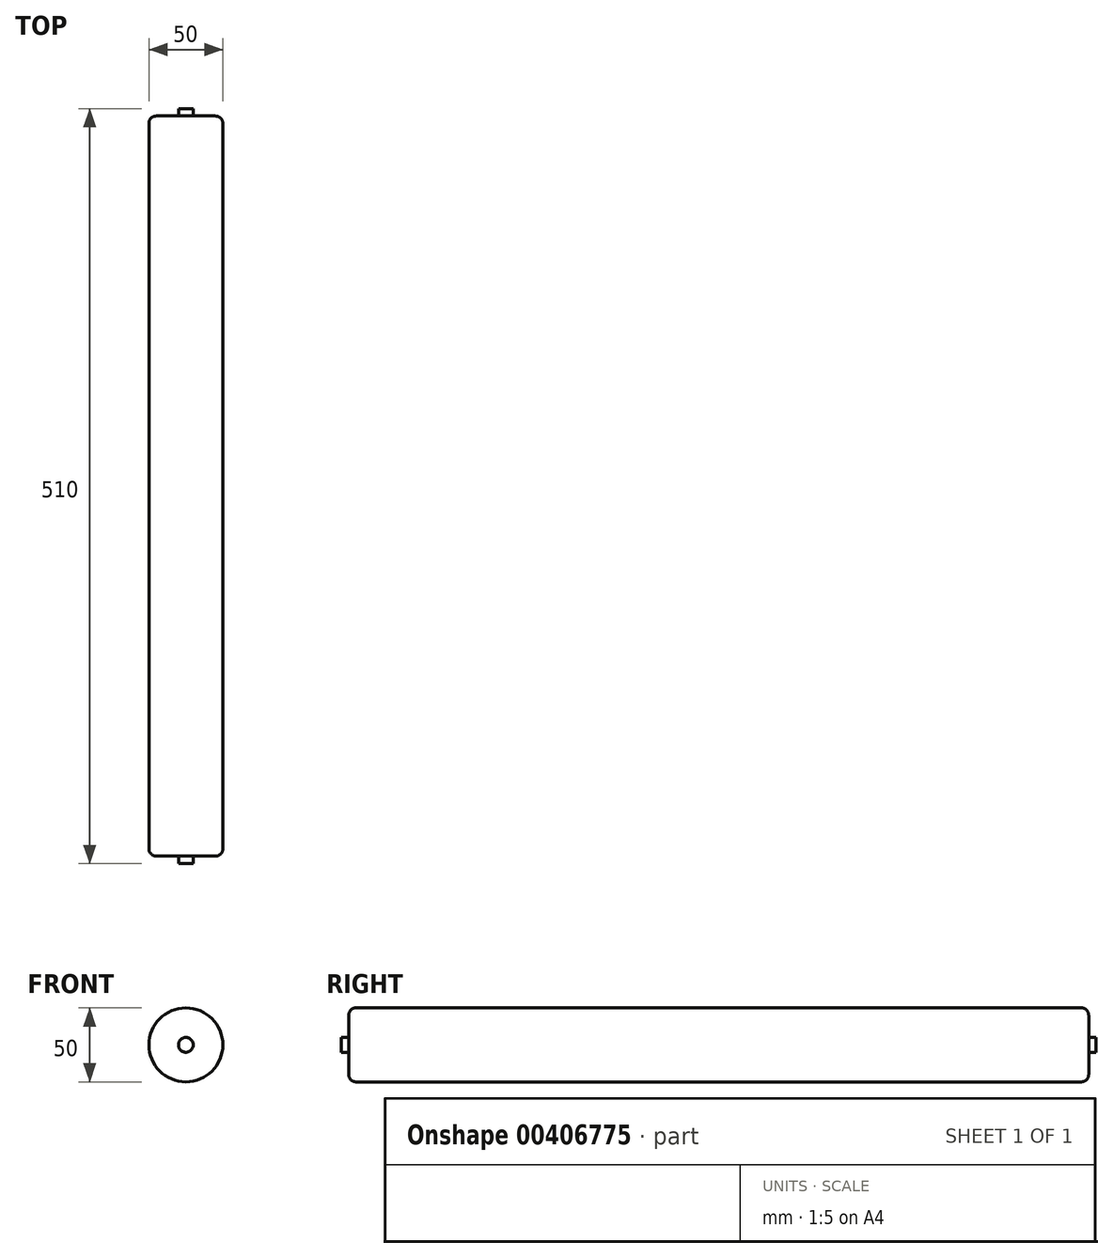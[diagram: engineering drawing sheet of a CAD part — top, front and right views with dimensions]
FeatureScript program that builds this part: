
annotation { "Feature Type Name" : "Feature", "Feature Type Description" : "" }
export const myFeature = defineFeature(function(context is Context, id is Id, definition is map)
    precondition{}
    {
        {
            var Q0;
            Q0=qCreatedBy(makeId("Front.planeOp"),FACE);
            var sketch = newSketch(context, id + "F0", { "sketchPlane" : qUnion([Q0])});
            skCircle(sketch, "E0", {"center": v(41.25, 34.25) * mm, "radius": 25 * mm});
            skSolve(sketch);
        }
        {
            var Q0;
            Q0=makeQuery(id+"F0.imprint","IMPRINT",FACE,{"disambiguationData":[TD([[makeQuery(id+"F0.imprint","IMPRINT",EDGE,{"derivedFrom":sQuery(id+"F0.wireOp",EDGE,"E0")}),1.0]])]});
            extrude(context, id + "F1", {"entities" : qUnion([Q0]), "depth" : 500 * mm});
        }
        {
            var Q0;
            Q0=makeQuery(id+"F1.opExtrude","CAP_FACE",FACE,{"disambiguationData":[OSD([sQuery(id+"F0.wireOp",EDGE,"E0")])],"isStart":true});
            var sketch = newSketch(context, id + "F2", { "sketchPlane" : qUnion([Q0])});
            skCircle(sketch, "E1", {"center": v(-41.25, 34.25) * mm, "radius": 5 * mm});
            skSolve(sketch);
        }
        {
            var Q0;
            Q0=makeQuery(id+"F2.imprint","IMPRINT",FACE,{"disambiguationData":[TD([[makeQuery(id+"F2.imprint","IMPRINT",EDGE,{"derivedFrom":sQuery(id+"F2.wireOp",EDGE,"E1")}),1.0]])]});
            extrude(context, id + "F3", {"entities" : qUnion([Q0]), "operationType" : NewBodyOperationType.ADD, "depth" : 5 * mm});
        }
        {
            var Q0;
            Q0=makeQuery(id+"F1.opExtrude","CAP_FACE",FACE,{"disambiguationData":[OSD([sQuery(id+"F0.wireOp",EDGE,"E0")])],"isStart":false});
            var sketch = newSketch(context, id + "F4", { "sketchPlane" : qUnion([Q0])});
            skCircle(sketch, "E2", {"center": v(41.25, 34.25) * mm, "radius": 5 * mm});
            skSolve(sketch);
        }
        {
            var Q0;
            Q0=makeQuery(id+"F4.imprint","IMPRINT",FACE,{"disambiguationData":[TD([[makeQuery(id+"F4.imprint","IMPRINT",EDGE,{"derivedFrom":sQuery(id+"F4.wireOp",EDGE,"E2")}),1.0]])]});
            extrude(context, id + "F5", {"entities" : qUnion([Q0]), "operationType" : NewBodyOperationType.ADD, "depth" : 5 * mm});
        }
        {
            var Q0;
            Q0=makeQuery(id+"F1.opExtrude","CAP_EDGE",EDGE,{"disambiguationData":[OSD([sQuery(id+"F0.wireOp",EDGE,"E0")])],"isStart":true});
            fillet(context, id + "F6", {"entities" : qUnion([Q0]), "radius" : 5 * mm, "tangentPropagation" : true, "allowEdgeOverflow" : false});
        }
        {
            var Q0;
            Q0=makeQuery(id+"F1.opExtrude","CAP_EDGE",EDGE,{"disambiguationData":[OSD([sQuery(id+"F0.wireOp",EDGE,"E0")])],"isStart":false});
            fillet(context, id + "F7", {"entities" : qUnion([Q0]), "radius" : 5 * mm, "tangentPropagation" : true, "allowEdgeOverflow" : false});
        }
    });
